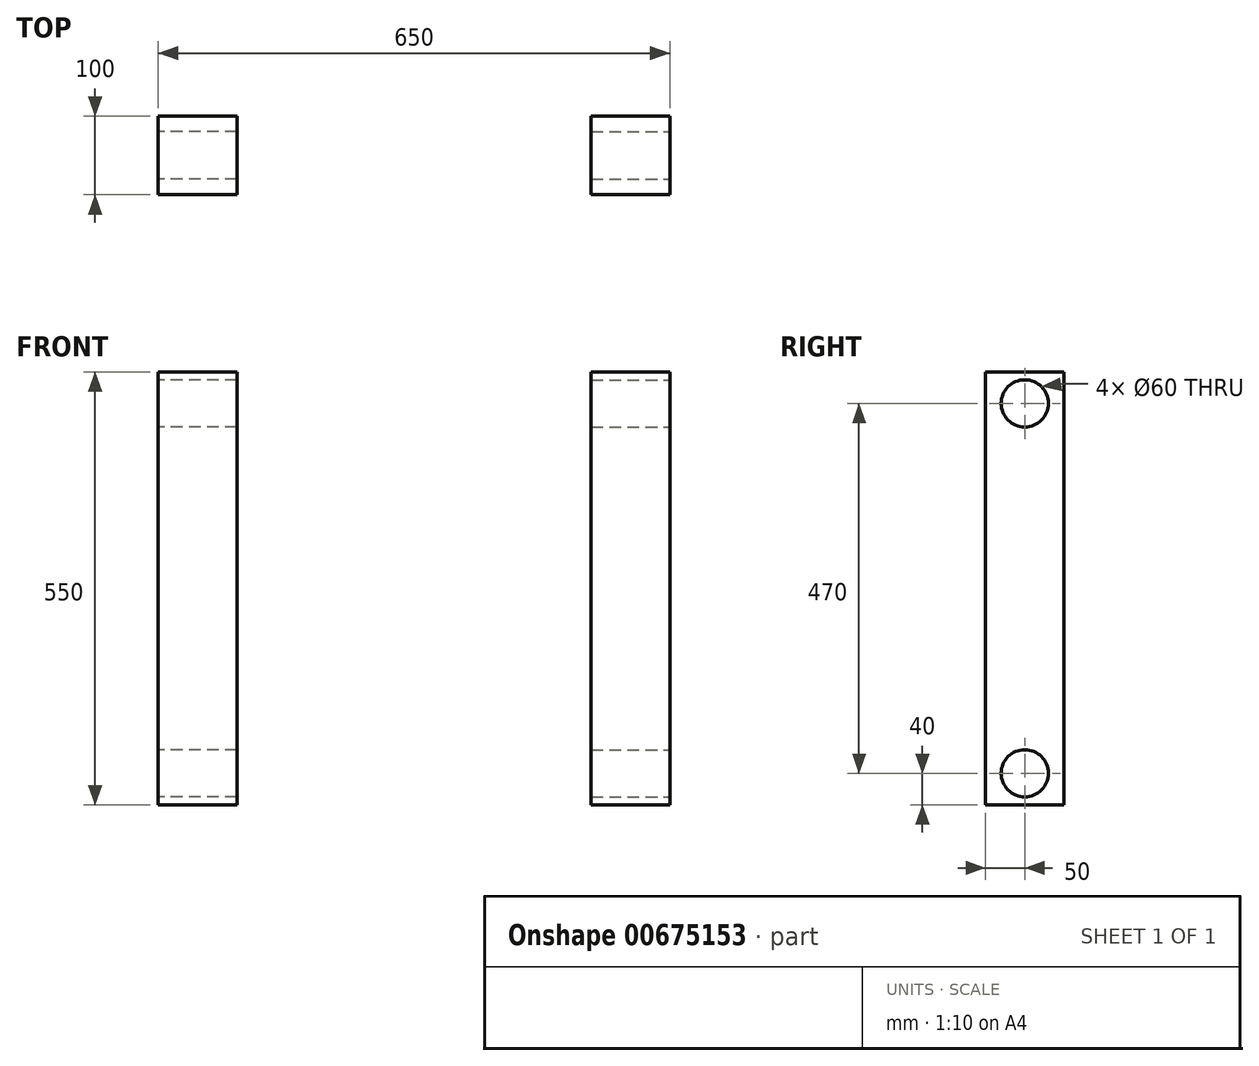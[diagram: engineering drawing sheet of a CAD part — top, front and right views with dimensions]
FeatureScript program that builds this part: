
annotation { "Feature Type Name" : "Feature", "Feature Type Description" : "" }
export const myFeature = defineFeature(function(context is Context, id is Id, definition is map)
    precondition{}
    {
        {
            var Q0;
            Q0=qCreatedBy(makeId("Top.planeOp"),FACE);
            var sketch = newSketch(context, id + "F0", { "sketchPlane" : qUnion([Q0])});
            skLineSegment(sketch, "E0.bottom", {"start": v(-325, 50) * mm, "end": v(-225, 50) * mm});
            skLineSegment(sketch, "E0.top", {"start": v(-325, -50) * mm, "end": v(-225, -50) * mm});
            skLineSegment(sketch, "E0.left", {"start": v(-325, 50) * mm, "end": v(-325, -50) * mm});
            skLineSegment(sketch, "E0.right", {"start": v(-225, 50) * mm, "end": v(-225, -50) * mm});
            skLineSegment(sketch, "E1.bottom", {"start": v(225, 50) * mm, "end": v(325, 50) * mm});
            skLineSegment(sketch, "E1.top", {"start": v(225, -50) * mm, "end": v(325, -50) * mm});
            skLineSegment(sketch, "E1.left", {"start": v(225, 50) * mm, "end": v(225, -50) * mm});
            skLineSegment(sketch, "E1.right", {"start": v(325, 50) * mm, "end": v(325, -50) * mm});
            skSolve(sketch);
        }
        {
            var Q0;
            Q0=makeQuery(id+"F0.imprint","IMPRINT",FACE,{"disambiguationData":[TD([[makeQuery(id+"F0.imprint","IMPRINT",EDGE,{"derivedFrom":sQuery(id+"F0.wireOp",EDGE,"E0.bottom")}),-1.0]])]});
            var Q1;
            Q1=makeQuery(id+"F0.imprint","IMPRINT",FACE,{"disambiguationData":[TD([[makeQuery(id+"F0.imprint","IMPRINT",EDGE,{"derivedFrom":sQuery(id+"F0.wireOp",EDGE,"E1.bottom")}),-1.0]])]});
            extrude(context, id + "F1", {"entities" : qUnion([Q0, Q1]), "depth" : 550 * mm, "offsetDistance" : 25 * mm});
        }
        {
            var Q0;
            Q0=makeQuery(id+"F1.opExtrude","SWEPT_FACE",FACE,{"disambiguationData":[OSD([sQuery(id+"F0.wireOp",EDGE,"E0.left")])]});
            var sketch = newSketch(context, id + "F2", { "sketchPlane" : qUnion([Q0])});
            skCircle(sketch, "E2", {"center": v(0, 510) * mm, "radius": 30 * mm});
            skSolve(sketch);
        }
        {
            var Q0;
            Q0=makeQuery(id+"F2.imprint","IMPRINT",FACE,{"disambiguationData":[TD([[makeQuery(id+"F2.imprint","IMPRINT",EDGE,{"derivedFrom":sQuery(id+"F2.wireOp",EDGE,"E2")}),1.0]])]});
            extrude(context, id + "F3", {"entities" : qUnion([Q0]), "operationType" : NewBodyOperationType.REMOVE, "oppositeDirection" : true, "depth" : 100 * mm, "offsetDistance" : 25 * mm});
        }
        {
            var Q0;
            Q0=makeQuery(id+"F1.opExtrude","SWEPT_FACE",FACE,{"disambiguationData":[OSD([sQuery(id+"F0.wireOp",EDGE,"E1.right")])]});
            var sketch = newSketch(context, id + "F4", { "sketchPlane" : qUnion([Q0])});
            skCircle(sketch, "E3", {"center": v(0, 510) * mm, "radius": 30 * mm});
            skSolve(sketch);
        }
        {
            var Q0;
            Q0=makeQuery(id+"F4.imprint","IMPRINT",FACE,{"disambiguationData":[TD([[makeQuery(id+"F4.imprint","IMPRINT",EDGE,{"derivedFrom":sQuery(id+"F4.wireOp",EDGE,"E3")}),1.0]])]});
            extrude(context, id + "F5", {"entities" : qUnion([Q0]), "operationType" : NewBodyOperationType.REMOVE, "oppositeDirection" : true, "depth" : 100 * mm, "offsetDistance" : 25 * mm});
        }
        {
            var Q0;
            Q0=makeQuery(id+"F1.opExtrude","SWEPT_FACE",FACE,{"disambiguationData":[OSD([sQuery(id+"F0.wireOp",EDGE,"E1.right")])]});
            var sketch = newSketch(context, id + "F6", { "sketchPlane" : qUnion([Q0])});
            skCircle(sketch, "E4", {"center": v(0, 40) * mm, "radius": 30 * mm});
            skSolve(sketch);
        }
        {
            var Q0;
            Q0=makeQuery(id+"F6.imprint","IMPRINT",FACE,{"disambiguationData":[TD([[makeQuery(id+"F6.imprint","IMPRINT",EDGE,{"derivedFrom":sQuery(id+"F6.wireOp",EDGE,"E4")}),1.0]])]});
            extrude(context, id + "F7", {"entities" : qUnion([Q0]), "operationType" : NewBodyOperationType.REMOVE, "oppositeDirection" : true, "depth" : 100 * mm, "offsetDistance" : 25 * mm});
        }
        {
            var Q0;
            Q0=makeQuery(id+"F1.opExtrude","SWEPT_FACE",FACE,{"disambiguationData":[OSD([sQuery(id+"F0.wireOp",EDGE,"E0.left")])]});
            var sketch = newSketch(context, id + "F8", { "sketchPlane" : qUnion([Q0])});
            skCircle(sketch, "E5", {"center": v(0, 40) * mm, "radius": 30 * mm});
            skSolve(sketch);
        }
        {
            var Q0;
            Q0=makeQuery(id+"F8.imprint","IMPRINT",FACE,{"disambiguationData":[TD([[makeQuery(id+"F8.imprint","IMPRINT",EDGE,{"derivedFrom":sQuery(id+"F8.wireOp",EDGE,"E5")}),1.0]])]});
            extrude(context, id + "F9", {"entities" : qUnion([Q0]), "operationType" : NewBodyOperationType.REMOVE, "oppositeDirection" : true, "depth" : 100 * mm, "offsetDistance" : 25 * mm});
        }
    });
